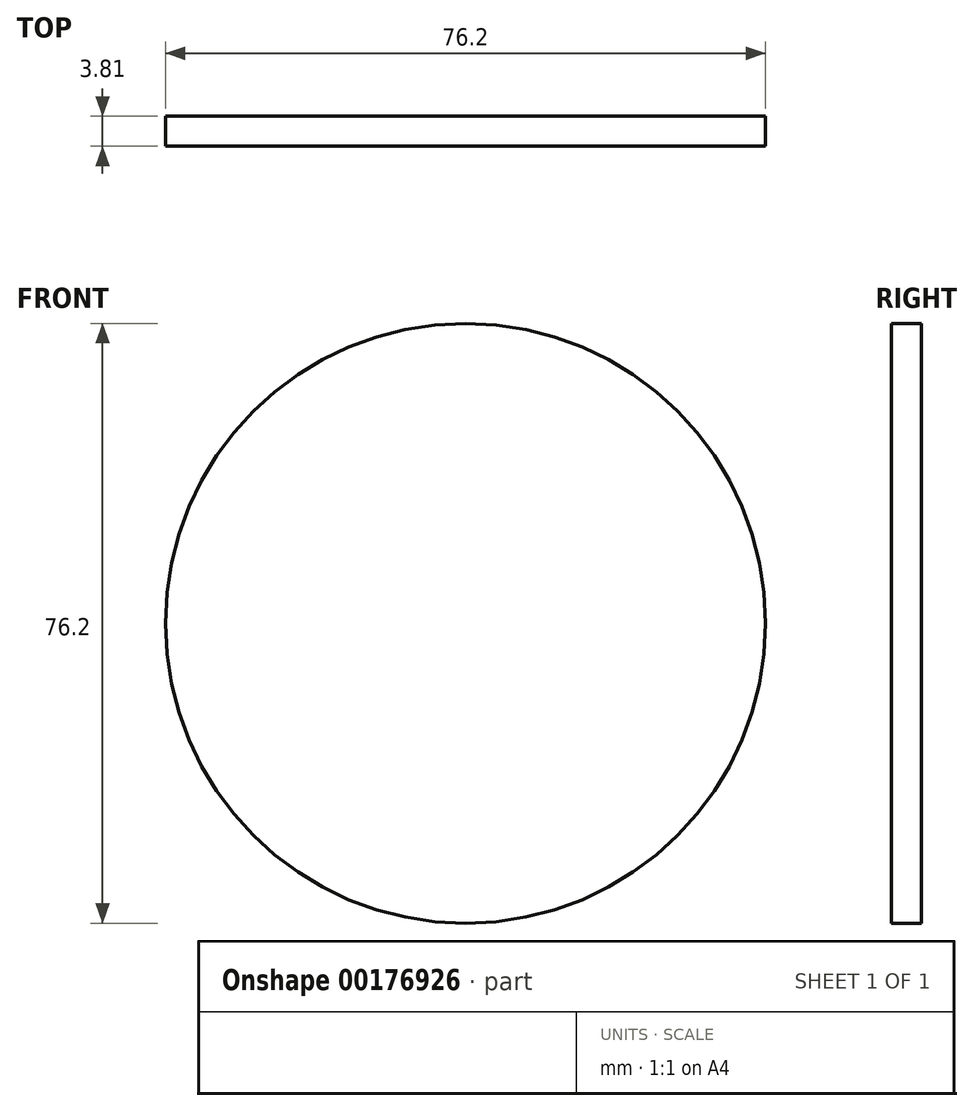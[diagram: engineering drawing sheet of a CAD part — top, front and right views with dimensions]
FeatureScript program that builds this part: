
annotation { "Feature Type Name" : "Feature", "Feature Type Description" : "" }
export const myFeature = defineFeature(function(context is Context, id is Id, definition is map)
    precondition{}
    {
        {
            var Q0;
            Q0=qCreatedBy(makeId("Front.planeOp"),FACE);
            var sketch = newSketch(context, id + "F0", { "sketchPlane" : qUnion([Q0])});
            skCircle(sketch, "E0", {"center": v(0, 0) * mm, "radius": 38.1 * mm});
            skSolve(sketch);
        }
        {
            var Q0;
            Q0 = qSketchRegion(id + "F0", true);
            extrude(context, id + "F1", {"entities" : qUnion([Q0]), "depth" : 3.8 * mm});
        }
    });
